FCSTD DOCUMENT  (FreeCAD 0.18R16110 (Git))
Label: cadpronto
License: All rights reserved
LicenseURL: http://en.wikipedia.org/wiki/All_rights_reserved
objects: Sketcher::SketchObject×1
note: 1 computed .brp shape members not serialized (recipe doc carries the construction recipe); baked Part::Feature solids carry a one-line shape summary decoded from their .brp

FEATURE [Sketcher::SketchObject] Sketch
  sketch-geometry (17):
    g0: LineSegment StartX=-58.2931 StartY=41.3834 StartZ=0 EndX=-15.2931 EndY=41.3834 EndZ=0
    g1: LineSegment StartX=-15.2931 StartY=41.3834 StartZ=0 EndX=-15.2931 EndY=-1.61659 EndZ=0
    g2: LineSegment StartX=-15.2931 StartY=-1.61659 StartZ=0 EndX=-58.2931 EndY=-1.61659 EndZ=0
    g3: LineSegment StartX=-58.2931 StartY=-1.61659 StartZ=0 EndX=-58.2931 EndY=41.3834 EndZ=0
    g4: LineSegment StartX=9.26032 StartY=41.8001 StartZ=0 EndX=50.2603 EndY=41.8001 EndZ=0
    g5: LineSegment StartX=50.2603 StartY=41.8001 StartZ=0 EndX=50.2603 EndY=0.800105 EndZ=0
    g6: LineSegment StartX=50.2603 StartY=0.800105 StartZ=0 EndX=9.26032 EndY=0.800105 EndZ=0
    g7: LineSegment StartX=9.26032 StartY=0.800105 StartZ=0 EndX=9.26032 EndY=41.8001 EndZ=0
    g8: LineSegment StartX=9.26032 StartY=21.1766 StartZ=0 EndX=9.26032 EndY=23.3766 EndZ=0
    g9: LineSegment StartX=9.21241 StartY=25.8113 StartZ=0 EndX=12.5503 EndY=23.3766 EndZ=0
    g10: LineSegment StartX=9.19599 StartY=18.9155 StartZ=0 EndX=12.5588 EndY=21.1766 EndZ=0
    g11: LineSegment StartX=9.26032 StartY=23.3766 StartZ=0 EndX=12.5503 EndY=23.3766 EndZ=0
    g12: LineSegment StartX=9.26032 StartY=21.1766 StartZ=0 EndX=12.5588 EndY=21.1766 EndZ=0
    g13: LineSegment StartX=50.24 StartY=25.0917 StartZ=0 EndX=47.4599 EndY=23.3766 EndZ=0
    g14: LineSegment StartX=47.4599 StartY=23.3766 StartZ=0 EndX=50.24 EndY=23.3766 EndZ=0
    g15: LineSegment StartX=50.24 StartY=21.1766 StartZ=0 EndX=47.5144 EndY=21.1766 EndZ=0
    g16: LineSegment StartX=47.5144 StartY=21.1766 StartZ=0 EndX=50.24 EndY=19.3134 EndZ=0
  constraints (19):
    c: Coincident(g0,g1)
    c: Coincident(g1,g2)
    c: Coincident(g2,g3)
    c: Coincident(g3,g0)
    c: Horizontal(g0)
    c: Horizontal(g2)
    c: Vertical(g1)
    c: Vertical(g3)
    c: Coincident(g4,g5)
    c: Coincident(g5,g6)
    c: Coincident(g6,g7)
    c: Coincident(g7,g4)
    c: Horizontal(g4)
    c: Horizontal(g6)
    c: Vertical(g5)
    c: Vertical(g7)
    c: Vertical(g8)
    c: Coincident(g13,g14)
    c: Coincident(g15,g16)
